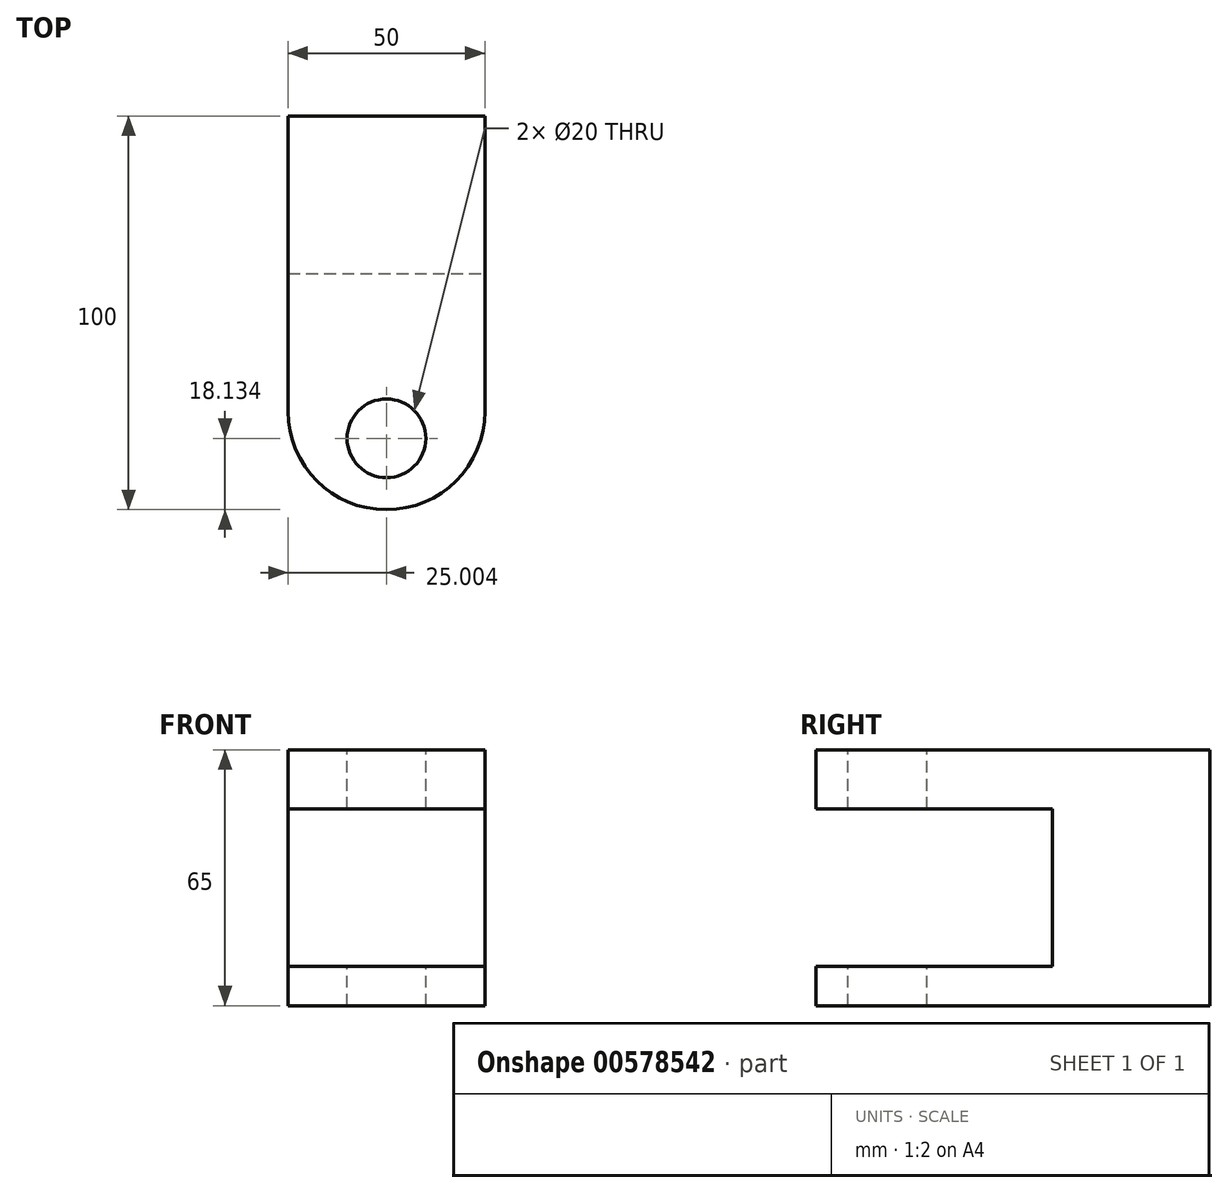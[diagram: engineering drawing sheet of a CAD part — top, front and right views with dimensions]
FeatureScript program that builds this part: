
annotation { "Feature Type Name" : "Feature", "Feature Type Description" : "" }
export const myFeature = defineFeature(function(context is Context, id is Id, definition is map)
    precondition{}
    {
        {
            var Q0;
            Q0=qCreatedBy(makeId("Front.planeOp"),FACE);
            var sketch = newSketch(context, id + "F0", { "sketchPlane" : qUnion([Q0])});
            skLineSegment(sketch, "E0.bottom", {"start": v(-23.52, 27.39) * mm, "end": v(26.48, 27.39) * mm});
            skLineSegment(sketch, "E0.top", {"start": v(-23.52, -37.61) * mm, "end": v(26.48, -37.61) * mm});
            skLineSegment(sketch, "E0.left", {"start": v(-23.52, 27.39) * mm, "end": v(-23.52, -37.61) * mm});
            skLineSegment(sketch, "E0.right", {"start": v(26.48, 27.39) * mm, "end": v(26.48, -37.61) * mm});
            skSolve(sketch);
        }
        {
            var Q0;
            Q0=makeQuery(id+"F0.imprint","IMPRINT",FACE,{"disambiguationData":[TD([[makeQuery(id+"F0.imprint","IMPRINT",EDGE,{"derivedFrom":sQuery(id+"F0.wireOp",EDGE,"E0.bottom")}),-1.0]])]});
            extrude(context, id + "F1", {"entities" : qUnion([Q0]), "depth" : 40 * mm, "offsetDistance" : 25 * mm});
        }
        {
            var Q0;
            Q0=makeQuery(id+"F1.opExtrude","CAP_FACE",FACE,{"disambiguationData":[OSD([sQuery(id+"F0.wireOp",EDGE,"E0.bottom"),sQuery(id+"F0.wireOp",EDGE,"E0.top"),sQuery(id+"F0.wireOp",EDGE,"E0.left"),sQuery(id+"F0.wireOp",EDGE,"E0.right")])],"isStart":false});
            var sketch = newSketch(context, id + "F2", { "sketchPlane" : qUnion([Q0])});
            skLineSegment(sketch, "E1.bottom", {"start": v(-23.52, 27.39) * mm, "end": v(26.48, 27.39) * mm});
            skLineSegment(sketch, "E1.top", {"start": v(-23.52, 12.39) * mm, "end": v(26.48, 12.39) * mm});
            skLineSegment(sketch, "E1.left", {"start": v(-23.52, 27.39) * mm, "end": v(-23.52, 12.39) * mm});
            skLineSegment(sketch, "E1.right", {"start": v(26.48, 27.39) * mm, "end": v(26.48, 12.39) * mm});
            skSolve(sketch);
        }
        {
            var Q0;
            Q0=makeQuery(id+"F2.imprint","IMPRINT",FACE,{"disambiguationData":[TD([[makeQuery(id+"F2.imprint","IMPRINT",EDGE,{"derivedFrom":sQuery(id+"F2.wireOp",EDGE,"E1.bottom")}),-1.0]])]});
            extrude(context, id + "F3", {"entities" : qUnion([Q0]), "operationType" : NewBodyOperationType.ADD, "depth" : 60 * mm, "offsetDistance" : 25 * mm});
        }
        {
            var Q0;
            Q0=makeQuery(id+"F1.opExtrude","CAP_FACE",FACE,{"disambiguationData":[OSD([sQuery(id+"F0.wireOp",EDGE,"E0.bottom"),sQuery(id+"F0.wireOp",EDGE,"E0.top"),sQuery(id+"F0.wireOp",EDGE,"E0.left"),sQuery(id+"F0.wireOp",EDGE,"E0.right")])],"isStart":false});
            var sketch = newSketch(context, id + "F4", { "sketchPlane" : qUnion([Q0])});
            skLineSegment(sketch, "E2.bottom", {"start": v(-23.52, -37.61) * mm, "end": v(26.48, -37.61) * mm});
            skLineSegment(sketch, "E2.top", {"start": v(-23.52, -27.61) * mm, "end": v(26.48, -27.61) * mm});
            skLineSegment(sketch, "E2.left", {"start": v(-23.52, -37.61) * mm, "end": v(-23.52, -27.61) * mm});
            skLineSegment(sketch, "E2.right", {"start": v(26.48, -37.61) * mm, "end": v(26.48, -27.61) * mm});
            skSolve(sketch);
        }
        {
            var Q0;
            Q0=makeQuery(id+"F4.imprint","IMPRINT",FACE,{"disambiguationData":[TD([[makeQuery(id+"F4.imprint","IMPRINT",EDGE,{"derivedFrom":sQuery(id+"F4.wireOp",EDGE,"E2.bottom")}),1.0]])]});
            extrude(context, id + "F5", {"entities" : qUnion([Q0]), "operationType" : NewBodyOperationType.ADD, "depth" : 60 * mm, "offsetDistance" : 25 * mm});
        }
        {
            var Q0;
            Q0=makeQuery(id+"F5.opExtrude","CAP_EDGE",EDGE,{"disambiguationData":[OSD([sQuery(id+"F4.wireOp",EDGE,"E2.left")])],"isStart":false});
            var Q1;
            Q1=makeQuery(id+"F3.opExtrude","CAP_EDGE",EDGE,{"disambiguationData":[OSD([sQuery(id+"F2.wireOp",EDGE,"E1.left")])],"isStart":false});
            var Q2;
            Q2=makeQuery(id+"F3.opExtrude","CAP_EDGE",EDGE,{"disambiguationData":[OSD([sQuery(id+"F2.wireOp",EDGE,"E1.right")])],"isStart":false});
            var Q3;
            Q3=makeQuery(id+"F5.opExtrude","CAP_EDGE",EDGE,{"disambiguationData":[OSD([sQuery(id+"F4.wireOp",EDGE,"E2.right")])],"isStart":false});
            fillet(context, id + "F6", {"entities" : qUnion([Q0, Q1, Q2, Q3]), "radius" : 25 * mm, "tangentPropagation" : true, "allowEdgeOverflow" : false});
        }
        {
            var Q0;
            Q0=makeQuery(id+"F3.boolean.opBoolean","MERGE",FACE,{"derivedFrom":[makeQuery(id+"F1.opExtrude","SWEPT_FACE",FACE,{"disambiguationData":[OSD([sQuery(id+"F0.wireOp",EDGE,"E0.bottom")])]}),makeQuery(id+"F3.opExtrude","SWEPT_FACE",FACE,{"disambiguationData":[OSD([sQuery(id+"F2.wireOp",EDGE,"E1.bottom")])]})]});
            var sketch = newSketch(context, id + "F7", { "sketchPlane" : qUnion([Q0])});
            skCircle(sketch, "E3", {"center": v(1.48, -81.87) * mm, "radius": 10 * mm});
            skSolve(sketch);
        }
        {
            var Q0;
            Q0=makeQuery(id+"F7.imprint","IMPRINT",FACE,{"disambiguationData":[TD([[makeQuery(id+"F7.imprint","IMPRINT",EDGE,{"derivedFrom":sQuery(id+"F7.wireOp",EDGE,"E3")}),1.0]])]});
            extrude(context, id + "F8", {"entities" : qUnion([Q0]), "operationType" : NewBodyOperationType.REMOVE, "oppositeDirection" : true, "depth" : 92.4 * mm, "offsetDistance" : 25 * mm});
        }
    });
